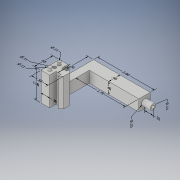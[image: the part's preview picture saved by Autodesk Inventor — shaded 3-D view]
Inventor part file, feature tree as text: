
AUTODESK INVENTOR PART (.ipt)
format: ipt  version: 2018 (Build 220112000, 112)  size: 200,704 bytes
history: native  units: in
note: dims shown in document units (in); Inventor stores cm internally (conversion verified against a paired STEP export)
features: other x17, sketch x7, extrude x5, hole x2
ambient origin geometry x8: Origin, YZ Plane, XZ Plane, XY Plane, X Axis, Y Axis, Z Axis, Center Point
bodies: Solid1 (feature_tree)
feature tree (31):
  other  "Annotations"
  extrude  "Extrusion1"  Depth=0.65in
  extrude  "Extrusion2"  Depth=0.28in
  hole  "Hole1"  [1 undecoded]
  extrude  "Extrusion3"  Depth=0.1in
  extrude  "Extrusion4"  Depth=1.0in
  extrude  "Extrusion5"  Depth=0.11in
  hole  "Hole2"  [1 undecoded]
  sketch  "Sketch1"  dims[d0=0.3in d1=0.65in]
  sketch  "Sketch2"  dims[d2=0.225in d3=0.28in]
  sketch  "Sketch3"  dims[d4=0.2in d5=0.1in]
  sketch  "Sketch4"  dims[d6=0.1in d7=0.1in]
  sketch  "Sketch5"  dims[d8=1.0in d9=0.0in d10=0.16in]
  sketch  "Sketch6"  dims[d11=0.16in d12=0.11in]
  sketch  "Sketch7"  dims[d13=0.11in d14=0.1in d15=0.0in d16=0.325in d17=0.11in d18=0.75in d19=0.375in d20=0.25in d21=0.5635in d22=0.45in d23=0.8108in d24=0.25in d25=0.4in d26=1.2in d27=0.0in d28=0.4in d29=1.75in d30=0.0in d31=0.2in d32=0.2in d33=0.3in d34=0.0in d35=0.11in d36=0.11in d37=0.75in d38=0.375in d39=0.25in d40=0.5635in d41=0.63in d42=0.8108in d100=0.0346in d101=-0.0319in d102=0.11in d103=0.7882in d104=0.2in d62=0.1213in d63=0.1055in d64=0.65in d65=0.1986in d66=0.1581in d67=0.58in d68=0.091in d69=0.0545in d70=0.3in d71=0.1724in d72=0.2363in d73=0.2in d74=0.2298in d75=0.2022in d76=1.0in d77=0.3738in d78=0.11in d79=0.049in d80=0.11in d81=2.002in d82=0.11in d83=0.1559in d84=0.1605in d85=0.4in d86=0.0944in d87=0.1006in d88=0.4in d89=0.1566in d90=0.3101in d91=2.0in d92=0.3451in d93=0.3309in d94=1.75in d95=0.0324in d96=0.2162in d97=1.2in d98=0.3in d99=1.8833in]
  other  "Linear Dimension 1"
  other  "Linear Dimension 2"
  other  "Linear Dimension 3"
  other  "Linear Dimension 4"
  other  "Linear Dimension 5"
  other  "Diameter Dimension 1"
  other  "Diameter Dimension 2"
  other  "Diameter Dimension 3"
  other  "Linear Dimension 6"
  other  "Linear Dimension 7"
  other  "Linear Dimension 8"
  other  "Linear Dimension 9"
  other  "Linear Dimension 10"
  other  "Linear Dimension 11"
  other  "Diameter Dimension 4"
  other  "Diameter Dimension 5"
note: 2 required parameter values undecoded (feature->parameter linkage not recoverable at this tier; creation-order binding heuristic only, values carry confidence <= 0.55)
